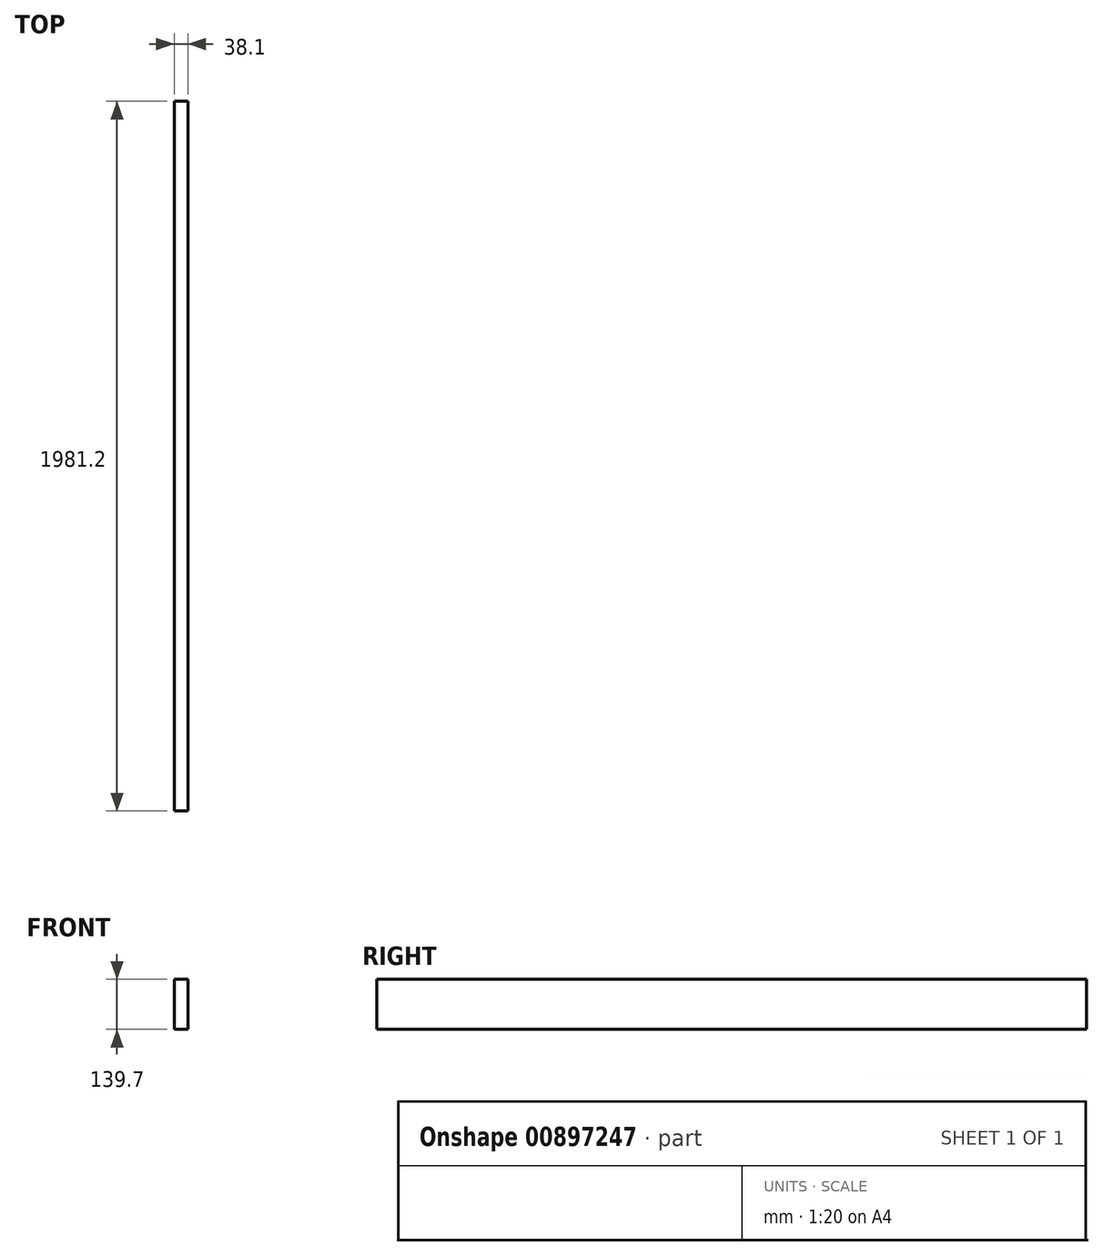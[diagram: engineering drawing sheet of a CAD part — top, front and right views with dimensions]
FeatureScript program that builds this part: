
annotation { "Feature Type Name" : "Feature", "Feature Type Description" : "" }
export const myFeature = defineFeature(function(context is Context, id is Id, definition is map)
    precondition{}
    {
        {
            var Q0;
            Q0=qCreatedBy(makeId("Front.planeOp"),FACE);
            var sketch = newSketch(context, id + "F0", { "sketchPlane" : qUnion([Q0])});
            skLineSegment(sketch, "E0.bottom", {"start": v(-19.05, 69.85) * mm, "end": v(19.05, 69.85) * mm});
            skLineSegment(sketch, "E0.top", {"start": v(-19.05, -69.85) * mm, "end": v(19.05, -69.85) * mm});
            skLineSegment(sketch, "E0.left", {"start": v(-19.05, 69.85) * mm, "end": v(-19.05, -69.85) * mm});
            skLineSegment(sketch, "E0.right", {"start": v(19.05, 69.85) * mm, "end": v(19.05, -69.85) * mm});
            skPoint(sketch, "E0.middle", {"position": v(0, 0) * mm});
            skSolve(sketch);
        }
        {
            var Q0;
            Q0=makeQuery(id+"F0.imprint","IMPRINT",FACE,{"disambiguationData":[TD([[makeQuery(id+"F0.imprint","IMPRINT",EDGE,{"derivedFrom":sQuery(id+"F0.wireOp",EDGE,"E0.bottom")}),-1.0]])]});
            extrude(context, id + "F1", {"entities" : qUnion([Q0]), "depth" : 1981.2 * mm, "offsetDistance" : 25.4 * mm});
        }
    });
